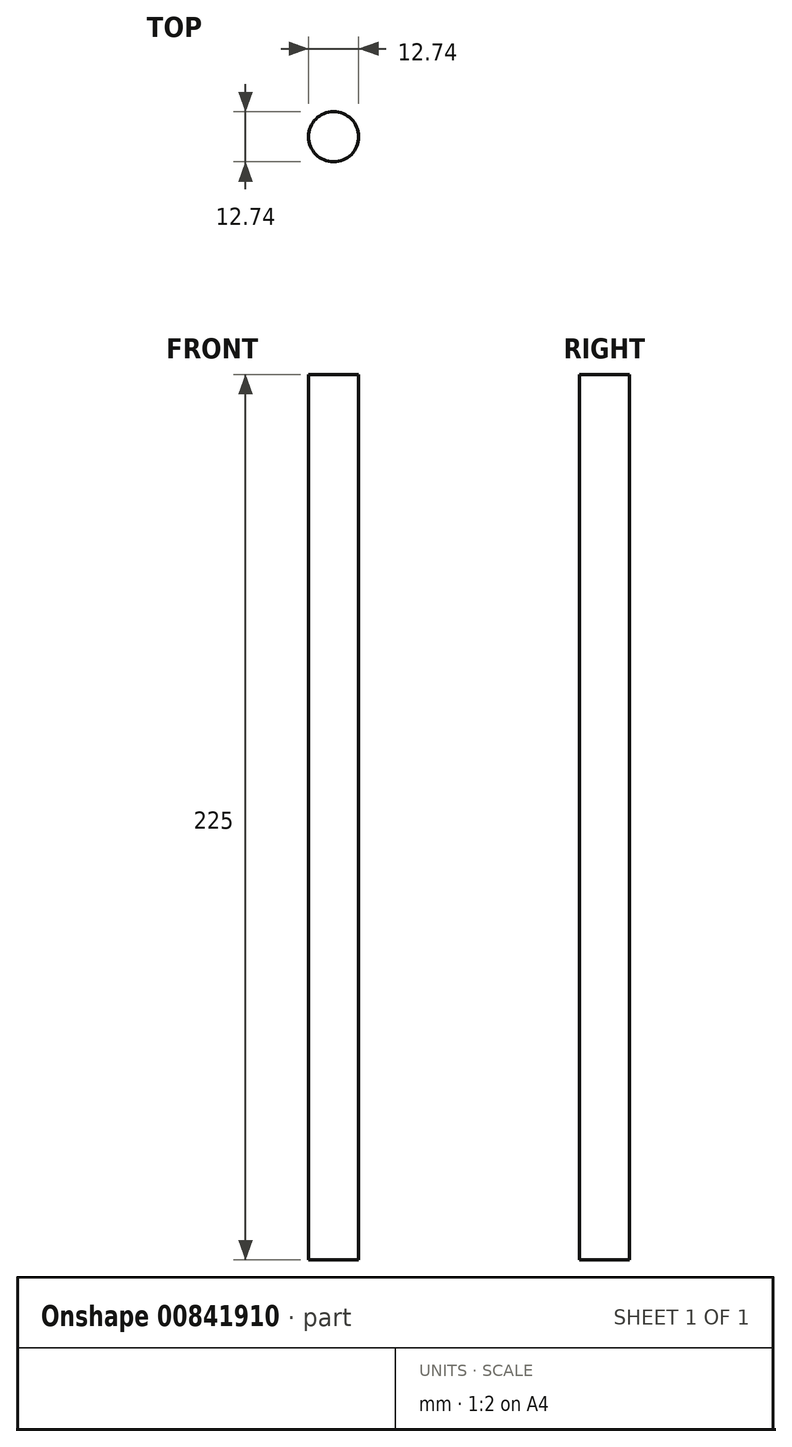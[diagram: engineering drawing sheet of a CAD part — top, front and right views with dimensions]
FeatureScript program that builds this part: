
annotation { "Feature Type Name" : "Feature", "Feature Type Description" : "" }
export const myFeature = defineFeature(function(context is Context, id is Id, definition is map)
    precondition{}
    {
        {
            var Q0;
            Q0=qCreatedBy(makeId("Top.planeOp"),FACE);
            var sketch = newSketch(context, id + "F0", { "sketchPlane" : qUnion([Q0])});
            skCircle(sketch, "E0", {"center": v(0, 0) * mm, "radius": 6.37 * mm});
            skSolve(sketch);
        }
        {
            var Q0;
            Q0 = qSketchRegion(id + "F0", true);
            extrude(context, id + "F1", {"entities" : qUnion([Q0]), "depth" : 225 * mm, "offsetDistance" : 25 * mm});
        }
    });
